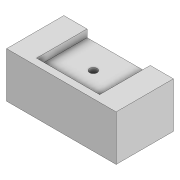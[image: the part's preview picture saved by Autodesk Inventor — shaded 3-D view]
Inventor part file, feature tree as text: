
AUTODESK INVENTOR PART (.ipt)
format: ipt  version: 2022 (Build 260153000, 153)  size: 154,624 bytes
history: native  units: mm
features: extrude x7, sketch x7, projected_geometry x7
ambient origin geometry x8: Origin, YZ Plane, XZ Plane, XY Plane, X Axis, Y Axis, Z Axis, Center Point
bodies: Volumenkörper1 (feature_tree)
feature tree (21):
  extrude  "Extrusion1"  Depth=13.0mm
  extrude  "Extrusion2"  Depth=7.5mm
  extrude  "Extrusion3"  Depth=6.0mm TaperAngle=0.0deg
  extrude  "Extrusion4"  Depth=6.8mm TaperAngle=0.0deg
  extrude  "Extrusion5"  Depth=4.0mm
  extrude  "Extrusion6"  Depth=10.0mm TaperAngle=0.0deg
  extrude  "Extrusion7"  Depth=10.0mm TaperAngle=0.0deg
  sketch  "Skizze1"  dims[d0=13.0mm d1=17.5mm]
  sketch  "Skizze2"  dims[d2=5.5mm d3=0.0mm d4=7.5mm]
  projected_geometry  "Projizierte Kontur1"
  sketch  "Skizze3"  dims[d5=6.0mm d6=1.0mm d7=0.0mm]
  projected_geometry  "Projizierte Kontur2"
  sketch  "Skizze4"  dims[d8=6.8mm d9=0.1mm d10=0.0mm]
  projected_geometry  "Projizierte Kontur3"
  sketch  "Skizze5"  dims[d11=7.3mm d12=4.0mm]
  projected_geometry  "Projizierte Kontur4"
  sketch  "Skizze6"  dims[d13=0.1mm d14=0.0mm d15=10.0mm d16=0.0mm]
  projected_geometry  "Projizierte Kontur5"
  sketch  "Skizze7"  dims[d17=0.8mm d18=10.0mm d19=0.0mm d20=10.0mm d21=0.0mm]
  projected_geometry  "Projizierte Kontur6"
  projected_geometry  "Projizierte Kontur7"
